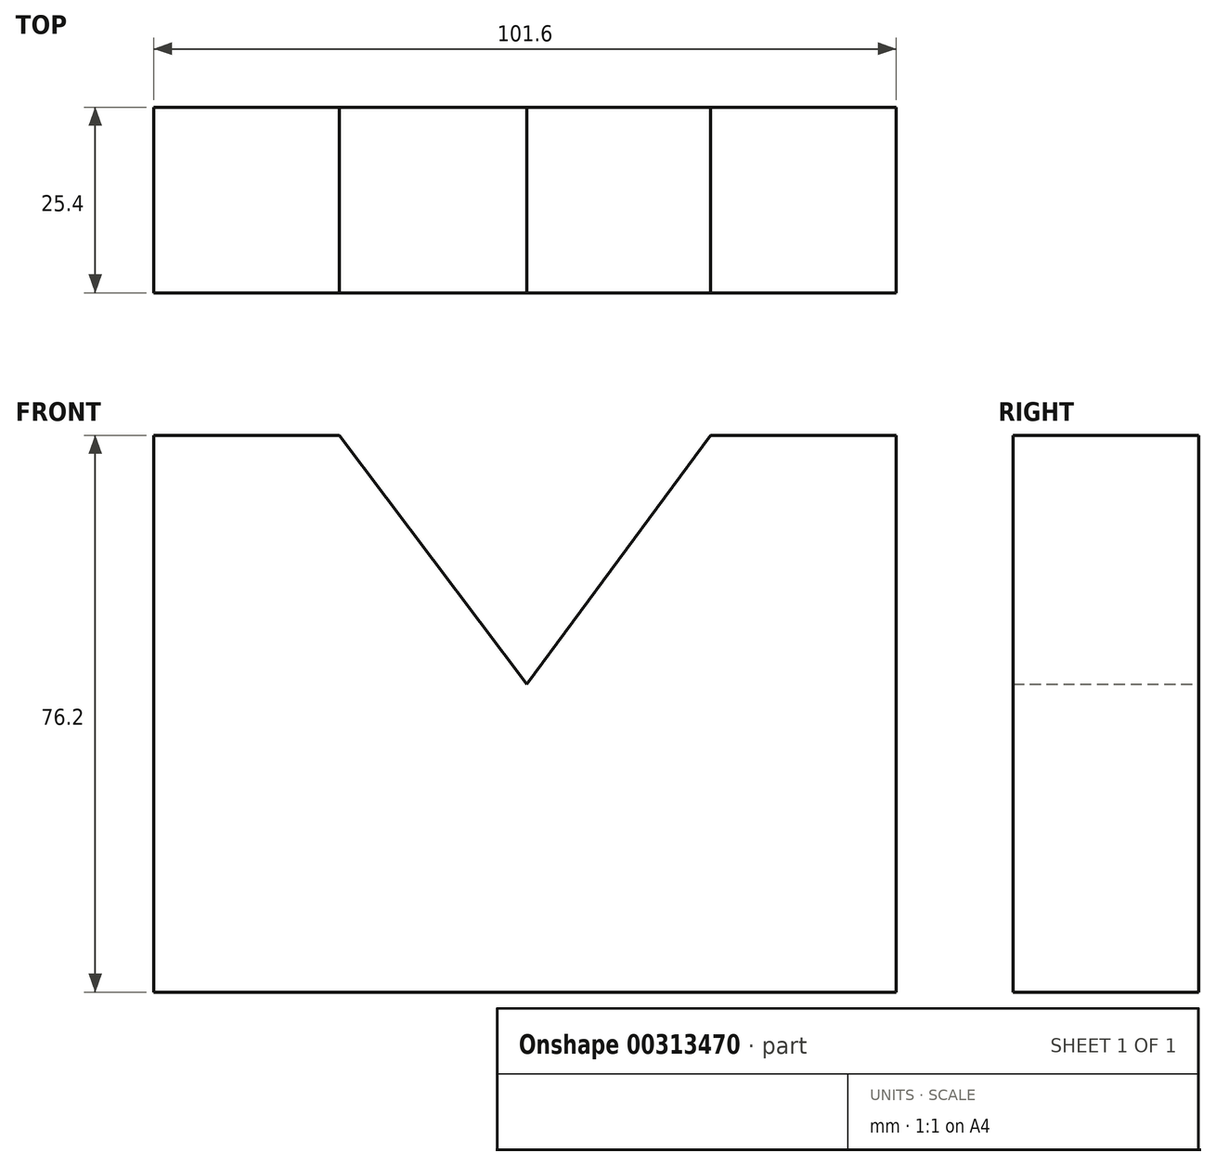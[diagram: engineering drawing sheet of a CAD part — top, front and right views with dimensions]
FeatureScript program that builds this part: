
annotation { "Feature Type Name" : "Feature", "Feature Type Description" : "" }
export const myFeature = defineFeature(function(context is Context, id is Id, definition is map)
    precondition{}
    {
        {
            var Q0;
            Q0=qCreatedBy(makeId("Front.planeOp"),FACE);
            var sketch = newSketch(context, id + "F0", { "sketchPlane" : qUnion([Q0])});
            skLineSegment(sketch, "E0", {"start": v(-51.08, 7.93) * mm, "end": v(-51.08, -68.27) * mm});
            skLineSegment(sketch, "E1", {"start": v(-51.08, -68.27) * mm, "end": v(50.52, -68.27) * mm});
            skLineSegment(sketch, "E2", {"start": v(50.52, -68.27) * mm, "end": v(50.52, 7.93) * mm});
            skLineSegment(sketch, "E3", {"start": v(50.52, 7.93) * mm, "end": v(25.12, 7.93) * mm});
            skLineSegment(sketch, "E4", {"start": v(-25.68, 7.93) * mm, "end": v(-51.08, 7.93) * mm});
            skPoint(sketch, "E5.startSnap0", {"position": v(-0.28, -68.27) * mm});
            skLineSegment(sketch, "E6", {"start": v(0, -26.1) * mm, "end": v(25.12, 7.93) * mm});
            skLineSegment(sketch, "E7", {"start": v(0, -26.1) * mm, "end": v(-25.68, 7.93) * mm});
            skSolve(sketch);
        }
        {
            var Q0;
            Q0 = qSketchRegion(id + "F0", true);
            extrude(context, id + "F1", {"entities" : qUnion([Q0]), "depth" : 25.4 * mm});
        }
    });
